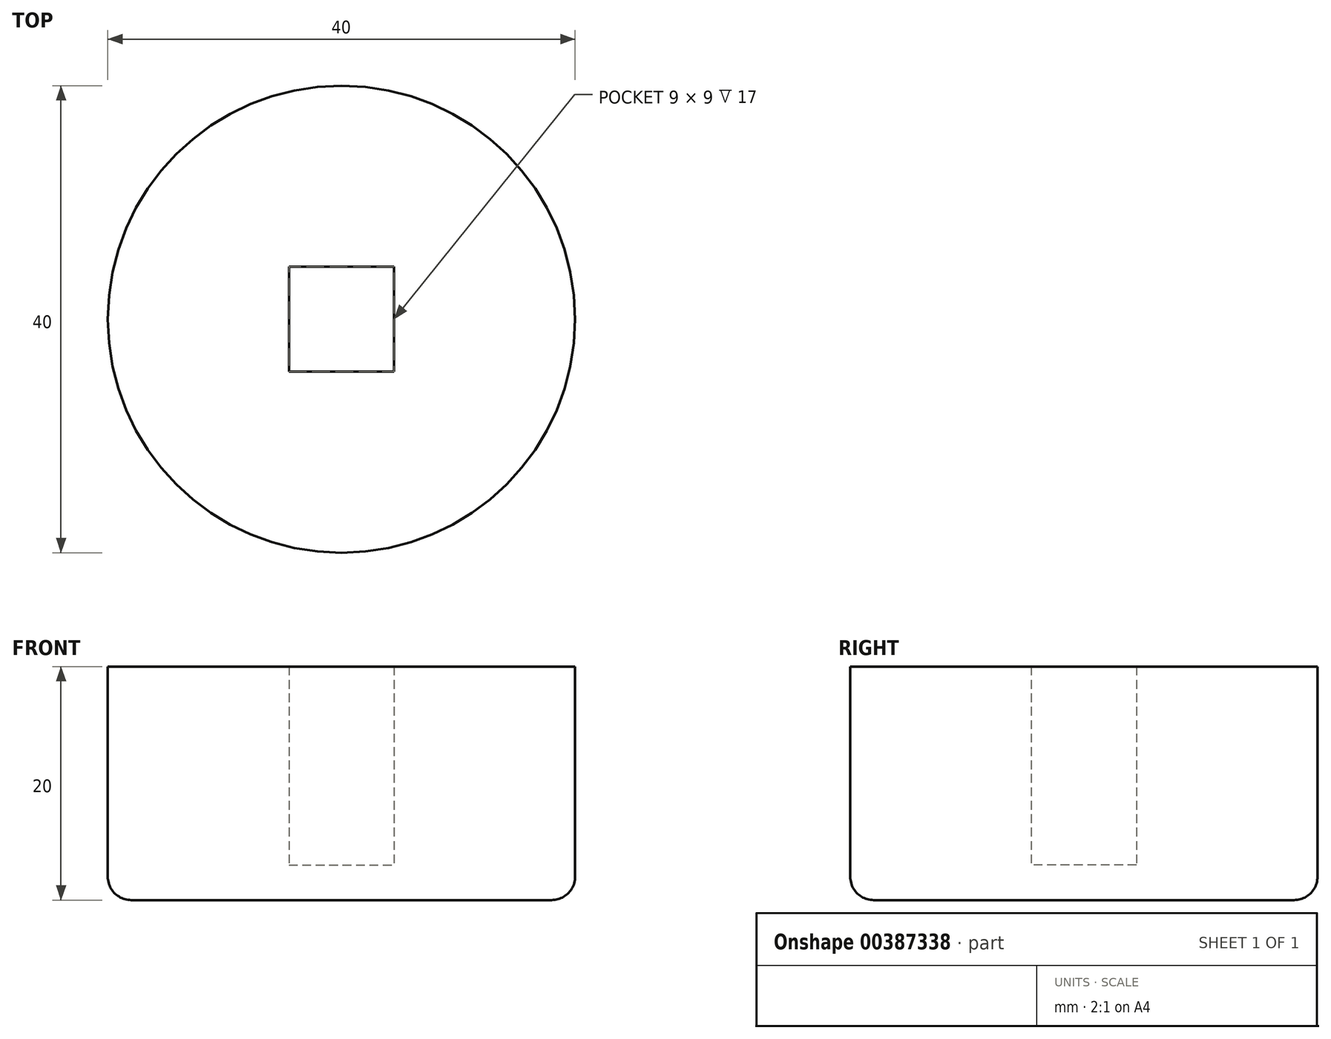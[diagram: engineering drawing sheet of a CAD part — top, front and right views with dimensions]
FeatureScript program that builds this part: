
annotation { "Feature Type Name" : "Feature", "Feature Type Description" : "" }
export const myFeature = defineFeature(function(context is Context, id is Id, definition is map)
    precondition{}
    {
        {
            var Q0;
            Q0=qCreatedBy(makeId("Top.planeOp"),FACE);
            var sketch = newSketch(context, id + "F0", { "sketchPlane" : qUnion([Q0])});
            skCircle(sketch, "E0", {"center": v(0, 0) * mm, "radius": 20 * mm});
            skLineSegment(sketch, "E1.bottom", {"start": v(4.5, -4.5) * mm, "end": v(-4.5, -4.5) * mm});
            skLineSegment(sketch, "E1.top", {"start": v(4.5, 4.5) * mm, "end": v(-4.5, 4.5) * mm});
            skLineSegment(sketch, "E1.left", {"start": v(4.5, -4.5) * mm, "end": v(4.5, 4.5) * mm});
            skLineSegment(sketch, "E1.right", {"start": v(-4.5, -4.5) * mm, "end": v(-4.5, 4.5) * mm});
            skSolve(sketch);
        }
        {
            var Q0;
            Q0 = qSketchRegion(id + "F0", true);
            var Q1;
            Q1=makeQuery(id+"F0.imprint","IMPRINT",FACE,{"disambiguationData":[TD([[makeQuery(id+"F0.imprint","IMPRINT",EDGE,{"derivedFrom":sQuery(id+"F0.wireOp",EDGE,"E1.bottom")}),-1.0]])]});
            extrude(context, id + "F1", {"entities" : qUnion([Q0, Q1]), "depth" : 3 * mm});
        }
        {
            var Q0;
            Q0=makeQuery(id+"F0.imprint","IMPRINT",FACE,{"disambiguationData":[TD([[makeQuery(id+"F0.imprint","IMPRINT",EDGE,{"derivedFrom":sQuery(id+"F0.wireOp",EDGE,"E0")}),1.0]])]});
            extrude(context, id + "F2", {"entities" : qUnion([Q0]), "operationType" : NewBodyOperationType.ADD, "depth" : 20 * mm});
        }
        {
            var Q0;
            Q0=makeQuery(id+"F1.opExtrude","CAP_EDGE",EDGE,{"disambiguationData":[OSD([sQuery(id+"F0.wireOp",EDGE,"E0")])],"isStart":true});
            fillet(context, id + "F3", {"entities" : qUnion([Q0]), "radius" : 2 * mm, "tangentPropagation" : true, "allowEdgeOverflow" : false});
        }
    });
